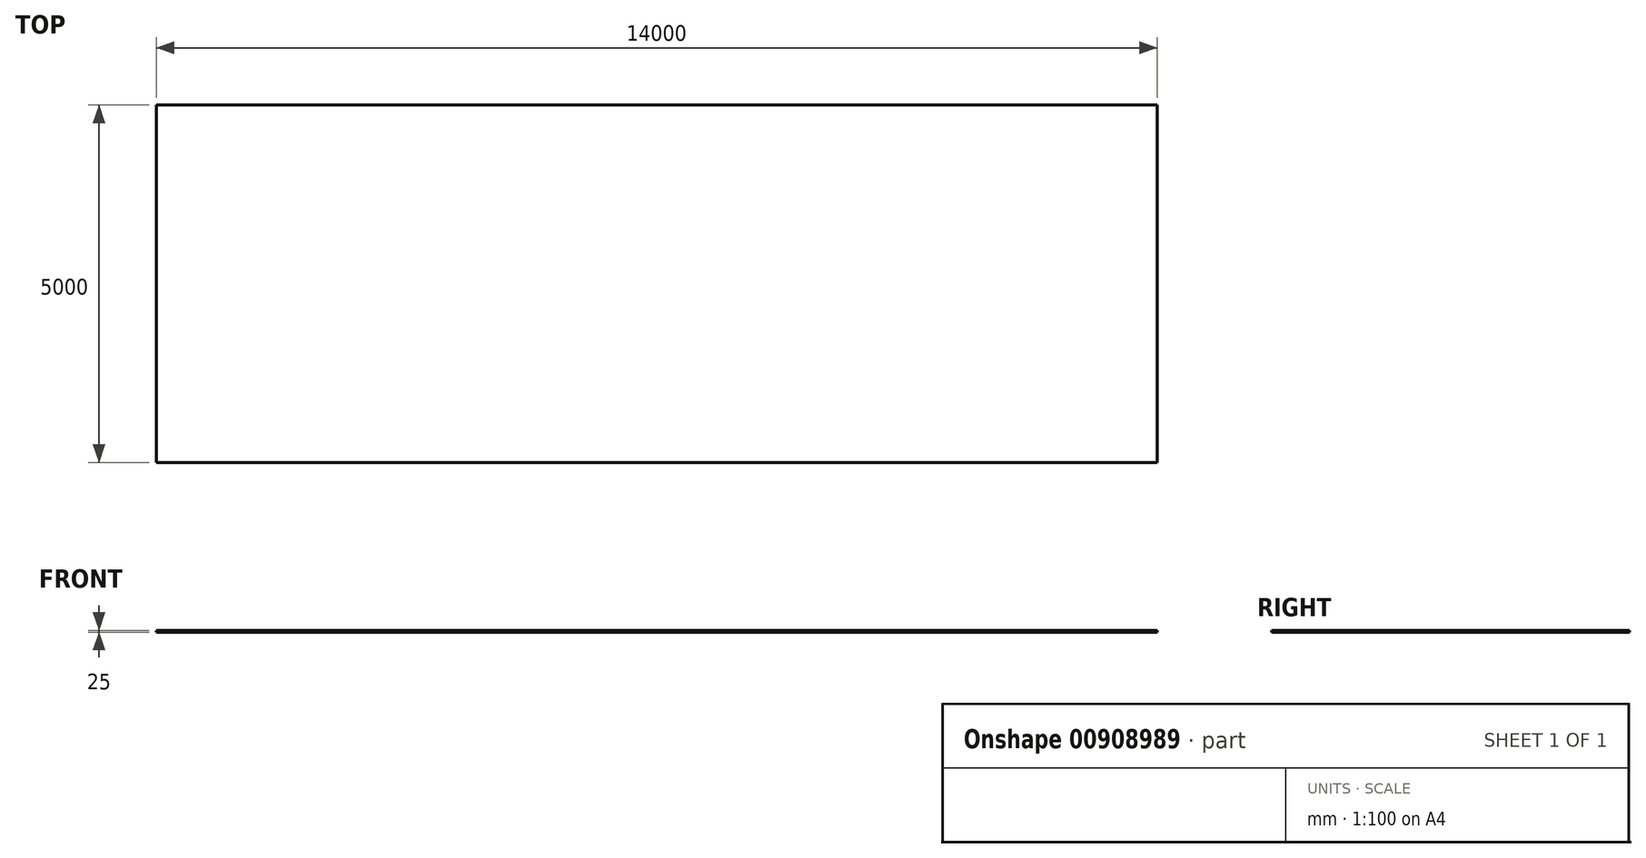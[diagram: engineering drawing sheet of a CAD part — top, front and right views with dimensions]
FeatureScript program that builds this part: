
annotation { "Feature Type Name" : "Feature", "Feature Type Description" : "" }
export const myFeature = defineFeature(function(context is Context, id is Id, definition is map)
    precondition{}
    {
        {
            var Q0;
            Q0=qCreatedBy(makeId("Top.planeOp"),FACE);
            var sketch = newSketch(context, id + "F0", { "sketchPlane" : qUnion([Q0])});
            skLineSegment(sketch, "E0.bottom", {"start": v(7000, -2500) * mm, "end": v(-7000, -2500) * mm});
            skLineSegment(sketch, "E0.top", {"start": v(7000, 2500) * mm, "end": v(-7000, 2500) * mm});
            skLineSegment(sketch, "E0.left", {"start": v(7000, -2500) * mm, "end": v(7000, 2500) * mm});
            skLineSegment(sketch, "E0.right", {"start": v(-7000, -2500) * mm, "end": v(-7000, 2500) * mm});
            skPoint(sketch, "E0.middle", {"position": v(0, 0) * mm});
            skSolve(sketch);
        }
        {
            var Q0;
            Q0 = qSketchRegion(id + "F0", true);
            extrude(context, id + "F1", {"entities" : qUnion([Q0]), "depth" : 25 * mm, "offsetDistance" : 25 * mm});
        }
    });
